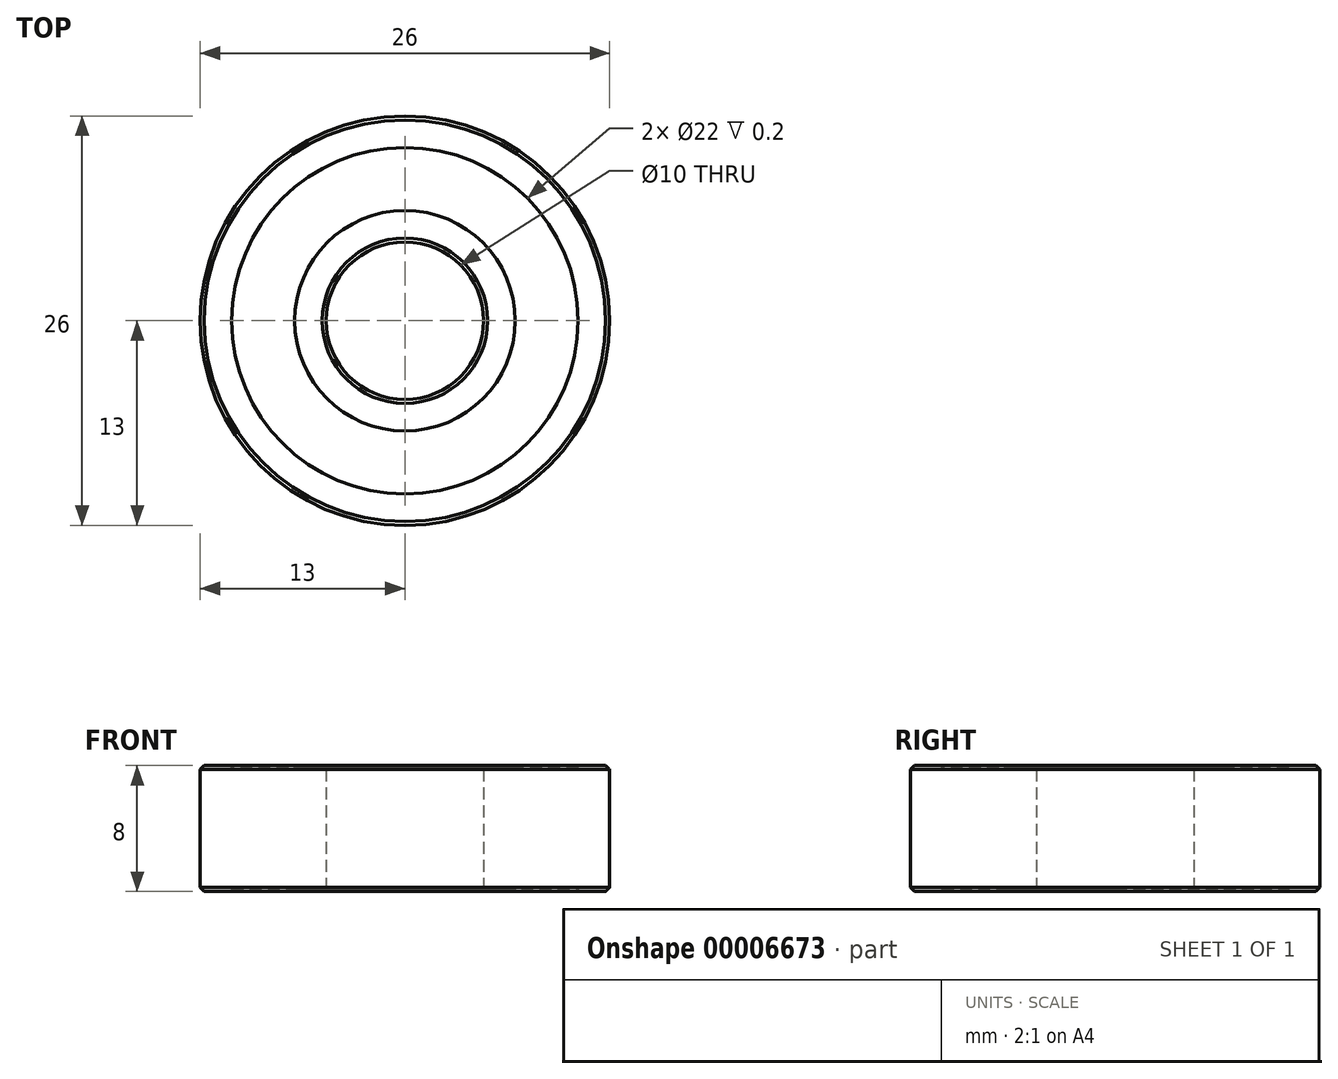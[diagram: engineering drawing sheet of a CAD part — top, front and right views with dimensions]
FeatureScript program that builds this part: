
annotation { "Feature Type Name" : "Feature", "Feature Type Description" : "" }
export const myFeature = defineFeature(function(context is Context, id is Id, definition is map)
    precondition{}
    {
        {
            var Q0;
            Q0=qCreatedBy(makeId("Top.planeOp"),FACE);
            var sketch = newSketch(context, id + "F0", { "sketchPlane" : qUnion([Q0])});
            skCircle(sketch, "E0", {"center": v(0, 0) * mm, "radius": 13 * mm});
            skCircle(sketch, "E1", {"center": v(0, 0) * mm, "radius": 5 * mm});
            skSolve(sketch);
        }
        {
            var Q0;
            Q0=qSketchRegion(id+"F0",true);
            extrude(context, id + "F1", {"entities" : qUnion([Q0]), "depth" : 8 * mm});
        }
        {
            var Q0;
            Q0=makeQuery(id+"F1.opExtrude","CAP_FACE",FACE,{"disambiguationData":[OSD([sQuery(id+"F0.wireOp",EDGE,"E0"),sQuery(id+"F0.wireOp",EDGE,"E1")])],"isStart":false});
            var sketch = newSketch(context, id + "F2", { "sketchPlane" : qUnion([Q0])});
            skCircle(sketch, "E2", {"center": v(0, 0) * mm, "radius": 7 * mm});
            skCircle(sketch, "E3", {"center": v(0, 0) * mm, "radius": 11 * mm});
            skSolve(sketch);
        }
        {
            var Q0;
            Q0=qSketchRegion(id+"F2",true);
            extrude(context, id + "F3", {"entities" : qUnion([Q0]), "operationType" : NewBodyOperationType.REMOVE, "oppositeDirection" : true, "depth" : 0.2 * mm});
        }
        {
            var Q0;
            Q0=makeQuery(id+"F1.opExtrude","CAP_EDGE",EDGE,{"disambiguationData":[OSD([sQuery(id+"F0.wireOp",EDGE,"E0")])],"isStart":false});
            var Q1;
            Q1=makeQuery(id+"F1.opExtrude","CAP_EDGE",EDGE,{"disambiguationData":[OSD([sQuery(id+"F0.wireOp",EDGE,"E1")])],"isStart":false});
            var Q2;
            Q2=makeQuery(id+"F1.opExtrude","CAP_EDGE",EDGE,{"disambiguationData":[OSD([sQuery(id+"F0.wireOp",EDGE,"E0")])],"isStart":true});
            var Q3;
            Q3=makeQuery(id+"F1.opExtrude","CAP_EDGE",EDGE,{"disambiguationData":[OSD([sQuery(id+"F0.wireOp",EDGE,"E1")])],"isStart":true});
            chamfer(context, id + "F4", {"entities" : qUnion([Q0, Q1, Q2, Q3]), "width" : 0.25 * mm, "tangentPropagation" : true});
        }
        {
            var Q0;
            Q0=makeQuery(id+"F1.opExtrude","CAP_FACE",FACE,{"disambiguationData":[OSD([sQuery(id+"F0.wireOp",EDGE,"E0"),sQuery(id+"F0.wireOp",EDGE,"E1")])],"isStart":true});
            var sketch = newSketch(context, id + "F5", { "sketchPlane" : qUnion([Q0])});
            skCircle(sketch, "E4", {"center": v(0, 0) * mm, "radius": 7 * mm});
            skCircle(sketch, "E5", {"center": v(0, 0) * mm, "radius": 11 * mm});
            skSolve(sketch);
        }
        {
            var Q0;
            Q0=qSketchRegion(id+"F5",true);
            extrude(context, id + "F6", {"entities" : qUnion([Q0]), "operationType" : NewBodyOperationType.REMOVE, "oppositeDirection" : true, "depth" : 0.2 * mm});
        }
    });
